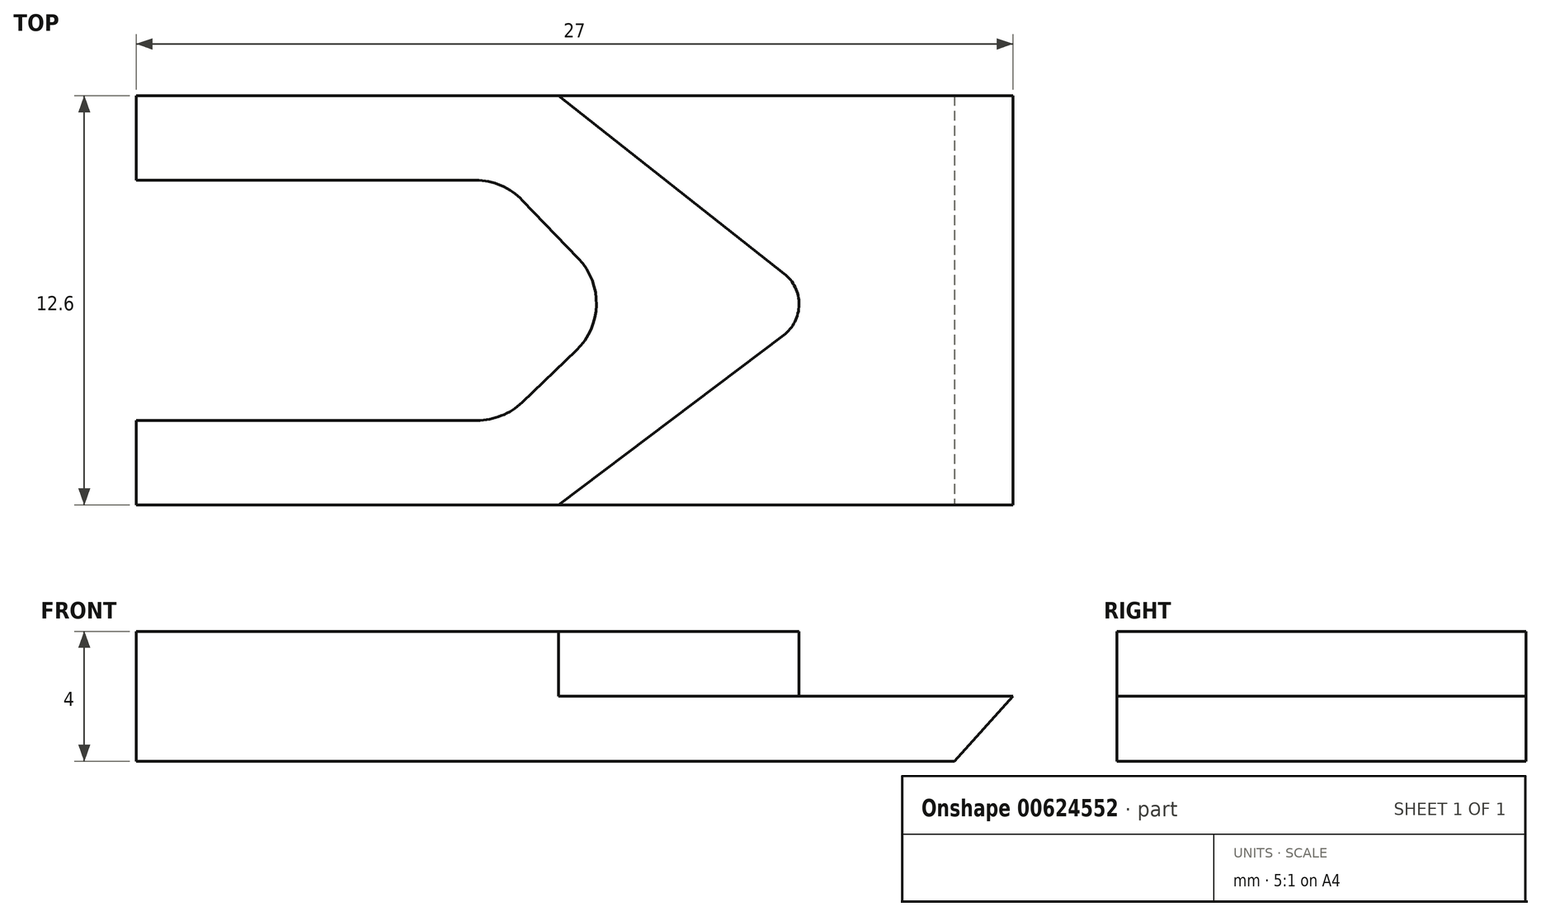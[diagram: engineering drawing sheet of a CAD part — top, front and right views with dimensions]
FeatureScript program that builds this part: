
annotation { "Feature Type Name" : "Feature", "Feature Type Description" : "" }
export const myFeature = defineFeature(function(context is Context, id is Id, definition is map)
    precondition{}
    {
        {
            var Q0;
            Q0=qCreatedBy(makeId("Top.planeOp"),FACE);
            var sketch = newSketch(context, id + "F0", { "sketchPlane" : qUnion([Q0])});
            skLineSegment(sketch, "E0.bottom", {"start": v(0, 0) * mm, "end": v(27, 0) * mm});
            skLineSegment(sketch, "E0.top", {"start": v(0, 12.6) * mm, "end": v(27, 12.6) * mm});
            skLineSegment(sketch, "E0.left", {"start": v(0, 0) * mm, "end": v(0, 12.6) * mm});
            skLineSegment(sketch, "E0.right", {"start": v(27, 0) * mm, "end": v(27, 12.6) * mm});
            skSolve(sketch);
        }
        {
            var Q0;
            Q0 = qSketchRegion(id + "F0", true);
            extrude(context, id + "F1", {"entities" : qUnion([Q0]), "depth" : 4 * mm, "offsetDistance" : 25 * mm});
        }
        {
            var Q0;
            Q0=makeQuery(id+"F1.opExtrude","CAP_FACE",FACE,{"disambiguationData":[OSD([sQuery(id+"F0.wireOp",EDGE,"E0.bottom"),sQuery(id+"F0.wireOp",EDGE,"E0.top"),sQuery(id+"F0.wireOp",EDGE,"E0.left"),sQuery(id+"F0.wireOp",EDGE,"E0.right")])],"isStart":false});
            var sketch = newSketch(context, id + "F2", { "sketchPlane" : qUnion([Q0])});
            skLineSegment(sketch, "E1", {"start": v(0, 10) * mm, "end": v(11.3, 10) * mm});
            skLineSegment(sketch, "E2", {"start": v(11.3, 10) * mm, "end": v(15, 6.14) * mm});
            skLineSegment(sketch, "E3", {"start": v(15, 6.14) * mm, "end": v(11.3, 2.6) * mm});
            skLineSegment(sketch, "E4", {"start": v(11.3, 2.6) * mm, "end": v(0, 2.6) * mm});
            skLineSegment(sketch, "E5", {"start": v(0, 2.6) * mm, "end": v(0, 10) * mm});
            skSolve(sketch);
        }
        {
            var Q0;
            Q0 = qSketchRegion(id + "F2", true);
            extrude(context, id + "F3", {"entities" : qUnion([Q0]), "operationType" : NewBodyOperationType.REMOVE, "oppositeDirection" : true, "depth" : 25 * mm, "offsetDistance" : 25 * mm});
        }
        {
            var Q0;
            Q0=makeQuery(id+"F3.boolean.opBoolean","COPY",EDGE,{"derivedFrom":makeQuery(id+"F3.opExtrude","SWEPT_EDGE",EDGE,{"disambiguationData":[OSD([sQuery(id+"F2.wireOp",EDGE,"E1"),sQuery(id+"F2.wireOp",EDGE,"E2")])]})});
            var Q1;
            Q1=makeQuery(id+"F3.boolean.opBoolean","COPY",EDGE,{"derivedFrom":makeQuery(id+"F3.opExtrude","SWEPT_EDGE",EDGE,{"disambiguationData":[OSD([sQuery(id+"F2.wireOp",EDGE,"E2"),sQuery(id+"F2.wireOp",EDGE,"E3")])]})});
            var Q2;
            Q2=makeQuery(id+"F3.boolean.opBoolean","COPY",EDGE,{"derivedFrom":makeQuery(id+"F3.opExtrude","SWEPT_EDGE",EDGE,{"disambiguationData":[OSD([sQuery(id+"F2.wireOp",EDGE,"E3"),sQuery(id+"F2.wireOp",EDGE,"E4")])]})});
            fillet(context, id + "F4", {"entities" : qUnion([Q0, Q1, Q2]), "radius" : 2 * mm, "tangentPropagation" : true, "allowEdgeOverflow" : false});
        }
        {
            var Q0;
            Q0=makeQuery(id+"F1.opExtrude","CAP_FACE",FACE,{"disambiguationData":[OSD([sQuery(id+"F0.wireOp",EDGE,"E0.bottom"),sQuery(id+"F0.wireOp",EDGE,"E0.top"),sQuery(id+"F0.wireOp",EDGE,"E0.left"),sQuery(id+"F0.wireOp",EDGE,"E0.right")])],"isStart":false});
            var sketch = newSketch(context, id + "F5", { "sketchPlane" : qUnion([Q0])});
            skLineSegment(sketch, "E6", {"start": v(13, 12.6) * mm, "end": v(19.95, 7.12) * mm});
            skPoint(sketch, "E6.endSnap0", {"position": v(14.17, 6.16) * mm});
            skLineSegment(sketch, "E7", {"start": v(19.93, 5.22) * mm, "end": v(13, 0) * mm});
            skPoint(sketch, "E8.visualSharp", {"position": v(21.18, 6.16) * mm});
            skArc(sketch, "E9.filletArc", {"start": v(19.93, 5.22) * mm, "mid": v(20.41, 6.17) * mm, "end": v(19.95, 7.12) * mm});
            skLineSegment(sketch, "E10", {"start": v(13, 12.6) * mm, "end": v(27, 12.6) * mm});
            skLineSegment(sketch, "E11", {"start": v(27, 12.6) * mm, "end": v(27, 0) * mm});
            skLineSegment(sketch, "E12", {"start": v(27, 0) * mm, "end": v(13, 0) * mm});
            skSolve(sketch);
        }
        {
            var Q0;
            Q0=makeQuery(id+"F5.imprint","IMPRINT",FACE,{"disambiguationData":[TD([[makeQuery(id+"F5.imprint","IMPRINT",EDGE,{"derivedFrom":sQuery(id+"F5.wireOp",EDGE,"E6")}),1.0]])]});
            extrude(context, id + "F6", {"entities" : qUnion([Q0]), "operationType" : NewBodyOperationType.REMOVE, "oppositeDirection" : true, "depth" : 2 * mm, "offsetDistance" : 25 * mm});
        }
        {
            var Q0;
            Q0=makeQuery(id+"F1.opExtrude","CAP_EDGE",EDGE,{"disambiguationData":[OSD([sQuery(id+"F0.wireOp",EDGE,"E0.right")])],"isStart":true});
            chamfer(context, id + "F7", {"entities" : qUnion([Q0]), "chamferType" : ChamferType.TWO_OFFSETS, "width1" : 1.8 * mm, "oppositeDirection" : false, "width2" : 2 * mm, "tangentPropagation" : true});
        }
    });
